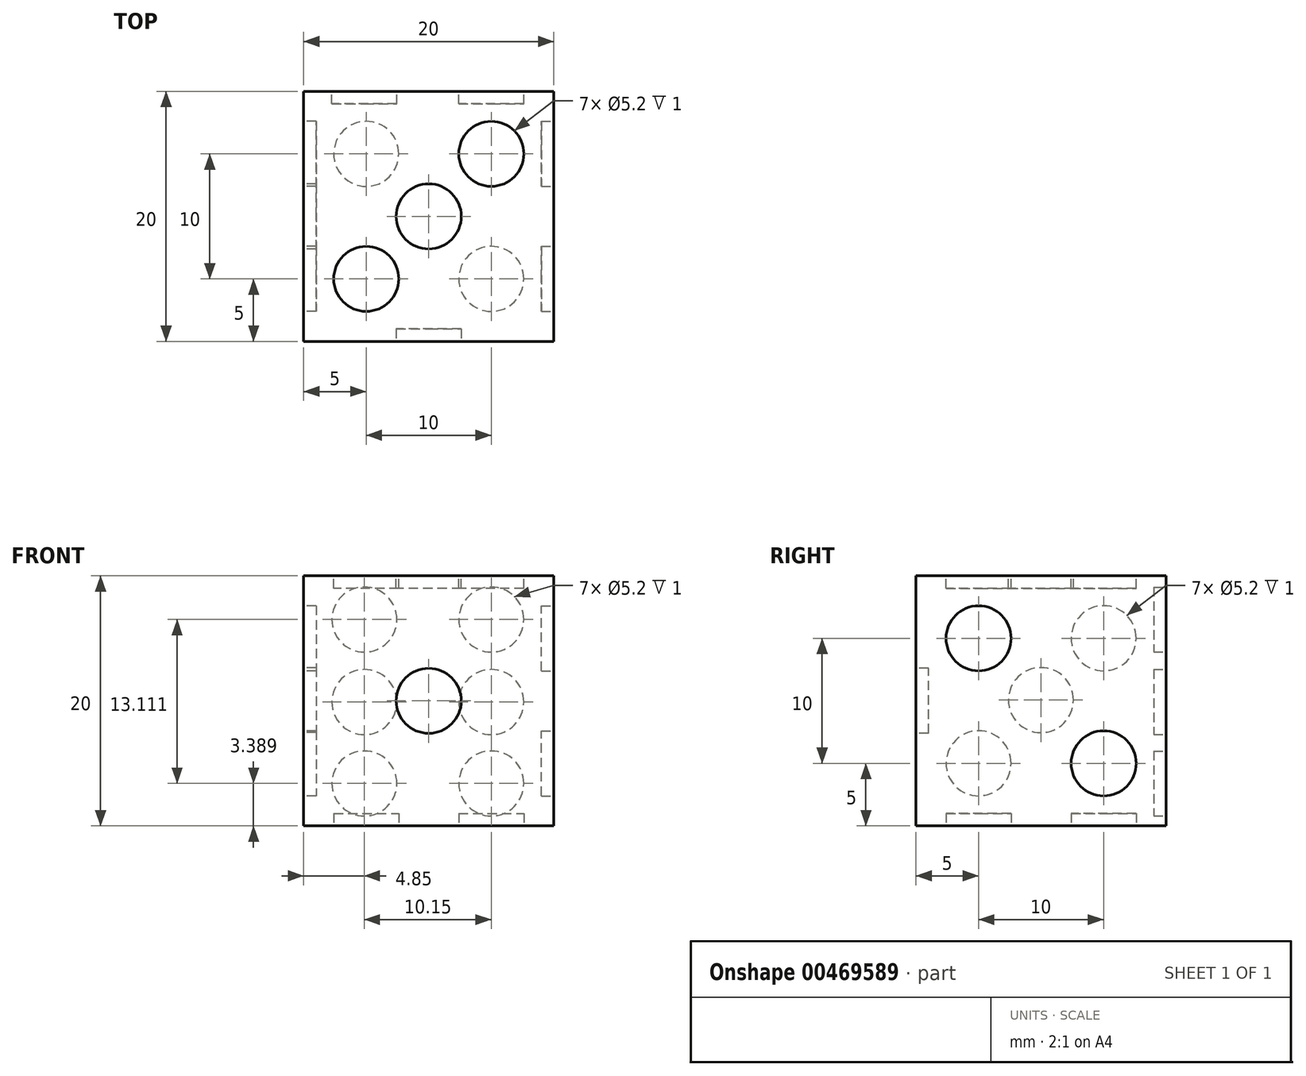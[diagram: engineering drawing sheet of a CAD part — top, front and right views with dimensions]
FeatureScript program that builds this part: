
annotation { "Feature Type Name" : "Feature", "Feature Type Description" : "" }
export const myFeature = defineFeature(function(context is Context, id is Id, definition is map)
    precondition{}
    {
        {
            var Q0;
            Q0=qCreatedBy(makeId("Front.planeOp"),FACE);
            var sketch = newSketch(context, id + "F0", { "sketchPlane" : qUnion([Q0])});
            skLineSegment(sketch, "E0.bottom", {"start": v(0, 0) * mm, "end": v(20, 0) * mm});
            skLineSegment(sketch, "E0.top", {"start": v(0, 20) * mm, "end": v(20, 20) * mm});
            skLineSegment(sketch, "E0.left", {"start": v(0, 0) * mm, "end": v(0, 20) * mm});
            skLineSegment(sketch, "E0.right", {"start": v(20, 0) * mm, "end": v(20, 20) * mm});
            skSolve(sketch);
        }
        {
            var Q0;
            Q0 = qSketchRegion(id + "F0", true);
            extrude(context, id + "F1", {"entities" : qUnion([Q0]), "depth" : 20 * mm});
        }
        {
            var Q0;
            Q0=makeQuery(id+"F1.opExtrude","CAP_FACE",FACE,{"disambiguationData":[OSD([sQuery(id+"F0.wireOp",EDGE,"E0.bottom"),sQuery(id+"F0.wireOp",EDGE,"E0.top"),sQuery(id+"F0.wireOp",EDGE,"E0.left"),sQuery(id+"F0.wireOp",EDGE,"E0.right")])],"isStart":false});
            var sketch = newSketch(context, id + "F2", { "sketchPlane" : qUnion([Q0])});
            skLineSegment(sketch, "E1", {"start": v(0, 20) * mm, "end": v(20, 0) * mm, "construction": true});
            skLineSegment(sketch, "E2", {"start": v(20, 20) * mm, "end": v(0, 0) * mm, "construction": true});
            skPoint(sketch, "E3.start.orphan", {"position": v(0, 10) * mm});
            skLineSegment(sketch, "E4", {"start": v(0, 10) * mm, "end": v(20, 10) * mm, "construction": true});
            skLineSegment(sketch, "E5", {"start": v(10, 20) * mm, "end": v(10, 0) * mm, "construction": true});
            skCircle(sketch, "E6", {"center": v(10, 10) * mm, "radius": 2.6 * mm});
            skSolve(sketch);
        }
        {
            var Q0;
            Q0=qCreatedBy(makeId("Front.planeOp"),FACE);
            var sketch = newSketch(context, id + "F3", { "sketchPlane" : qUnion([Q0])});
            skSolve(sketch);
        }
        {
            var Q0;
            Q0 = qSketchRegion(id + "F3", true);
            var Q1;
            Q1=makeQuery(id+"F2.imprint","IMPRINT",FACE,{"disambiguationData":[TD([[makeQuery(id+"F2.imprint","IMPRINT",EDGE,{"derivedFrom":sQuery(id+"F2.wireOp",EDGE,"E6")}),1.0]])]});
            extrude(context, id + "F4", {"entities" : qUnion([Q0, Q1]), "operationType" : NewBodyOperationType.REMOVE, "oppositeDirection" : true, "depth" : 1 * mm});
        }
        {
            var Q0;
            Q0=qCreatedBy(makeId("Front.planeOp"),FACE);
            var sketch = newSketch(context, id + "F5", { "sketchPlane" : qUnion([Q0])});
            skLineSegment(sketch, "E7", {"start": v(0, 0) * mm, "end": v(19.85, 19.89) * mm, "construction": true});
            skLineSegment(sketch, "E8", {"start": v(0, 19.8) * mm, "end": v(19.85, 0) * mm, "construction": true});
            skPoint(sketch, "E9.endSnap0", {"position": v(9.92, 9.94) * mm});
            skLineSegment(sketch, "E10", {"start": v(19.85, 9.94) * mm, "end": v(0, 9.94) * mm, "construction": true});
            skLineSegment(sketch, "E11", {"start": v(9.92, 19.89) * mm, "end": v(9.92, 0) * mm, "construction": true});
            skSolve(sketch);
        }
        {
            var Q0;
            Q0=makeQuery(id+"F1.opExtrude","CAP_FACE",FACE,{"disambiguationData":[OSD([sQuery(id+"F0.wireOp",EDGE,"E0.bottom"),sQuery(id+"F0.wireOp",EDGE,"E0.top"),sQuery(id+"F0.wireOp",EDGE,"E0.left"),sQuery(id+"F0.wireOp",EDGE,"E0.right")])],"isStart":true});
            var sketch = newSketch(context, id + "F6", { "sketchPlane" : qUnion([Q0])});
            skCircle(sketch, "E12", {"center": v(-15, 16.5) * mm, "radius": 2.6 * mm});
            skCircle(sketch, "E13.MirrorC", {"center": v(-4.85, 16.5) * mm, "radius": 2.6 * mm});
            skCircle(sketch, "E14.MirrorC", {"center": v(-15, 3.39) * mm, "radius": 2.6 * mm});
            skCircle(sketch, "E15.MirrorC", {"center": v(-4.85, 3.39) * mm, "radius": 2.6 * mm});
            skCircle(sketch, "E16", {"center": v(-15, 9.9) * mm, "radius": 2.6 * mm});
            skCircle(sketch, "E17.MirrorC", {"center": v(-4.85, 9.9) * mm, "radius": 2.6 * mm});
            skSolve(sketch);
        }
        {
            var Q0;
            Q0 = qSketchRegion(id + "F6", true);
            extrude(context, id + "F7", {"entities" : qUnion([Q0]), "operationType" : NewBodyOperationType.REMOVE, "oppositeDirection" : true, "depth" : 1 * mm});
        }
        {
            var Q0;
            Q0=makeQuery(id+"F1.opExtrude","SWEPT_FACE",FACE,{"disambiguationData":[OSD([sQuery(id+"F0.wireOp",EDGE,"E0.left")])]});
            var sketch = newSketch(context, id + "F8", { "sketchPlane" : qUnion([Q0])});
            skLineSegment(sketch, "E18", {"start": v(0, 20) * mm, "end": v(20, 0) * mm, "construction": true});
            skLineSegment(sketch, "E19", {"start": v(20, 20) * mm, "end": v(0, 0) * mm, "construction": true});
            skLineSegment(sketch, "E20", {"start": v(0, 10) * mm, "end": v(20, 10) * mm, "construction": true});
            skLineSegment(sketch, "E21", {"start": v(10, 20) * mm, "end": v(10, 0) * mm, "construction": true});
            skSolve(sketch);
        }
        {
            var Q0;
            {var subQ0=sQuery(id+"F0.wireOp",EDGE,"E0.left");Q0=makeQuery(id+"F8.imprint","IMPRINT",FACE,{"disambiguationData":[TD([[makeQuery(id+"F8.imprint","IMPRINT",EDGE,{"derivedFrom":makeQuery(id+"F1.opExtrude","CAP_EDGE",EDGE,{"disambiguationData":[OSD([subQ0])],"isStart":true})}),-1.0]])]});}
            var sketch = newSketch(context, id + "F9", { "sketchPlane" : qUnion([Q0])});
            skCircle(sketch, "E22", {"center": v(10.02, 10.06) * mm, "radius": 2.6 * mm});
            skCircle(sketch, "E23", {"center": v(5, 15) * mm, "radius": 2.6 * mm});
            skCircle(sketch, "E24.MirrorC", {"center": v(15, 5) * mm, "radius": 2.6 * mm});
            skCircle(sketch, "E25.MirrorC", {"center": v(5, 5) * mm, "radius": 2.6 * mm});
            skCircle(sketch, "E26.MirrorC", {"center": v(15, 15) * mm, "radius": 2.6 * mm});
            skSolve(sketch);
        }
        {
            var Q0;
            Q0 = qSketchRegion(id + "F9", true);
            extrude(context, id + "F10", {"entities" : qUnion([Q0]), "operationType" : NewBodyOperationType.REMOVE, "oppositeDirection" : true, "depth" : 1 * mm});
        }
        {
            var Q0;
            Q0=makeQuery(id+"F1.opExtrude","SWEPT_FACE",FACE,{"disambiguationData":[OSD([sQuery(id+"F0.wireOp",EDGE,"E0.right")])]});
            var sketch = newSketch(context, id + "F11", { "sketchPlane" : qUnion([Q0])});
            skCircle(sketch, "E27", {"center": v(-15, 15) * mm, "radius": 2.6 * mm});
            skCircle(sketch, "E28.MirrorC", {"center": v(-5, 5) * mm, "radius": 2.6 * mm});
            skSolve(sketch);
        }
        {
            var Q0;
            Q0 = qSketchRegion(id + "F11", true);
            extrude(context, id + "F12", {"entities" : qUnion([Q0]), "operationType" : NewBodyOperationType.REMOVE, "oppositeDirection" : true, "depth" : 1 * mm});
        }
        {
            var Q0;
            Q0=makeQuery(id+"F1.opExtrude","SWEPT_FACE",FACE,{"disambiguationData":[OSD([sQuery(id+"F0.wireOp",EDGE,"E0.top")])]});
            var sketch = newSketch(context, id + "F13", { "sketchPlane" : qUnion([Q0])});
            skLineSegment(sketch, "E29", {"start": v(0, 0) * mm, "end": v(20, -20) * mm, "construction": true});
            skLineSegment(sketch, "E30", {"start": v(20, 0) * mm, "end": v(0, -20) * mm, "construction": true});
            skLineSegment(sketch, "E31", {"start": v(0, -10) * mm, "end": v(20, -10) * mm, "construction": true});
            skLineSegment(sketch, "E32", {"start": v(10, 0) * mm, "end": v(10, -20) * mm, "construction": true});
            skCircle(sketch, "E33", {"center": v(10, -10) * mm, "radius": 2.6 * mm});
            skCircle(sketch, "E34", {"center": v(15, -5) * mm, "radius": 2.6 * mm});
            skCircle(sketch, "E35.MirrorC", {"center": v(5, -15) * mm, "radius": 2.6 * mm});
            skSolve(sketch);
        }
        {
            var Q0;
            Q0 = qSketchRegion(id + "F13", true);
            extrude(context, id + "F14", {"entities" : qUnion([Q0]), "operationType" : NewBodyOperationType.REMOVE, "oppositeDirection" : true, "depth" : 1 * mm});
        }
        {
            var Q0;
            Q0=makeQuery(id+"F1.opExtrude","SWEPT_FACE",FACE,{"disambiguationData":[OSD([sQuery(id+"F0.wireOp",EDGE,"E0.bottom")])]});
            var sketch = newSketch(context, id + "F15", { "sketchPlane" : qUnion([Q0])});
            skLineSegment(sketch, "E36", {"start": v(0, 0) * mm, "end": v(20, 20) * mm, "construction": true});
            skLineSegment(sketch, "E37", {"start": v(0, 20) * mm, "end": v(20, 0) * mm, "construction": true});
            skLineSegment(sketch, "E38", {"start": v(10, 20) * mm, "end": v(10, 0) * mm, "construction": true});
            skLineSegment(sketch, "E39", {"start": v(0, 10) * mm, "end": v(20, 10) * mm, "construction": true});
            skSolve(sketch);
        }
        {
            var Q0;
            Q0=qCreatedBy(makeId("Top.planeOp"),FACE);
            var sketch = newSketch(context, id + "F16", { "sketchPlane" : qUnion([Q0])});
            skCircle(sketch, "E40", {"center": v(5, -15) * mm, "radius": 2.6 * mm});
            skCircle(sketch, "E41.MirrorC", {"center": v(5, -5) * mm, "radius": 2.6 * mm});
            skCircle(sketch, "E42.MirrorC", {"center": v(15, -15) * mm, "radius": 2.6 * mm});
            skCircle(sketch, "E43.MirrorC", {"center": v(15, -5) * mm, "radius": 2.6 * mm});
            skSolve(sketch);
        }
        {
            var Q0;
            Q0 = qSketchRegion(id + "F16", true);
            extrude(context, id + "F17", {"entities" : qUnion([Q0]), "operationType" : NewBodyOperationType.REMOVE, "oppositeDirection" : true, "depth" : 1 * mm});
        }
        {
            var Q0;
            {var subQ0=sQuery(id+"F0.wireOp",EDGE,"E0.bottom");Q0=makeQuery(id+"F15.imprint","IMPRINT",FACE,{"disambiguationData":[TD([[makeQuery(id+"F15.imprint","IMPRINT",EDGE,{"derivedFrom":makeQuery(id+"F1.opExtrude","CAP_EDGE",EDGE,{"disambiguationData":[OSD([subQ0])],"isStart":true})}),1.0]])]});}
            var sketch = newSketch(context, id + "F18", { "sketchPlane" : qUnion([Q0])});
            skCircle(sketch, "E44", {"center": v(5, 15) * mm, "radius": 2.6 * mm});
            skCircle(sketch, "E45.MirrorC", {"center": v(5, 5) * mm, "radius": 2.6 * mm});
            skCircle(sketch, "E46.MirrorC", {"center": v(15, 15) * mm, "radius": 2.6 * mm});
            skCircle(sketch, "E47.MirrorC", {"center": v(15, 5) * mm, "radius": 2.6 * mm});
            skSolve(sketch);
        }
        {
            var Q0;
            Q0 = qSketchRegion(id + "F18", true);
            extrude(context, id + "F19", {"entities" : qUnion([Q0]), "operationType" : NewBodyOperationType.REMOVE, "oppositeDirection" : true, "depth" : 1 * mm});
        }
    });
